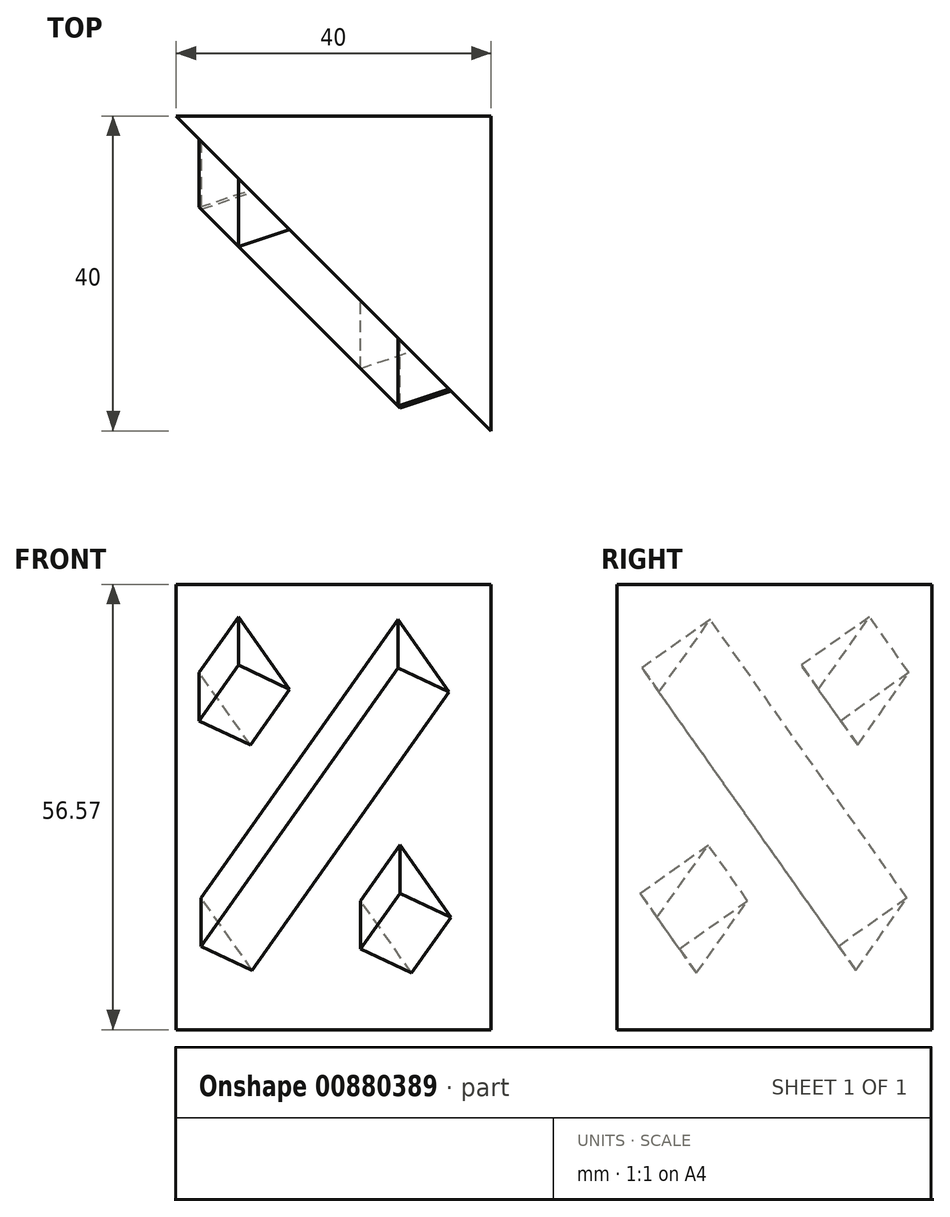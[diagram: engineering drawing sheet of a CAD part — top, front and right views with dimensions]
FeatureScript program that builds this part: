
annotation { "Feature Type Name" : "Feature", "Feature Type Description" : "" }
export const myFeature = defineFeature(function(context is Context, id is Id, definition is map)
    precondition{}
    {
        {
            var Q0;
            Q0=qCreatedBy(makeId("Top.planeOp"),FACE);
            var sketch = newSketch(context, id + "F0", { "sketchPlane" : qUnion([Q0])});
            skLineSegment(sketch, "E0.bottom", {"start": v(20, 20) * mm, "end": v(-20, 20) * mm});
            skLineSegment(sketch, "E0.top", {"start": v(20, -20) * mm, "end": v(-20, -20) * mm});
            skLineSegment(sketch, "E0.left", {"start": v(20, 20) * mm, "end": v(20, -20) * mm});
            skLineSegment(sketch, "E0.right", {"start": v(-20, 20) * mm, "end": v(-20, -20) * mm});
            skPoint(sketch, "E0.middle", {"position": v(0, 0) * mm});
            skLineSegment(sketch, "E1", {"start": v(-20, 20) * mm, "end": v(20, -20) * mm});
            skSolve(sketch);
        }
        {
            var Q0;
            Q0=makeQuery(id+"F0.imprint","IMPRINT",FACE,{"disambiguationData":[TD([[makeQuery(id+"F0.imprint","IMPRINT",EDGE,{"derivedFrom":sQuery(id+"F0.wireOp",EDGE,"E0.bottom")}),1.0]])]});
            extrude(context, id + "F1", {"entities" : qUnion([Q0]), "depth" : (40 * sqrt(2)) * mm, "offsetDistance" : 25 * mm});
        }
        {
            var Q0;
            Q0=makeQuery(id+"F1.opExtrude","SWEPT_FACE",FACE,{"disambiguationData":[OSD([sQuery(id+"F0.wireOp",EDGE,"E1")])]});
            var sketch = newSketch(context, id + "F2", { "sketchPlane" : qUnion([Q0])});
            skLineSegment(sketch, "E2", {"start": v(28.28, 0) * mm, "end": v(-28.28, 56.57) * mm});
            skSolve(sketch);
        }
        {
            var Q0;
            Q0=sQuery(id+"F2.wireOp",EDGE,"E2");
            var Q1;
            Q1=makeQuery(id+"F2.imprint","IMPRINT",FACE,{"disambiguationData":[TD([[makeQuery(id+"F2.imprint","IMPRINT",EDGE,{"derivedFrom":sQuery(id+"F2.wireOp",EDGE,"E2")}),-1.0]])]});
            cPlane(context, id + "F3", {"entities" : qUnion([Q0, Q1]), "cplaneType" : CPlaneType.LINE_ANGLE, "offset" : 25 * mm, "angle" : 90 * degree, "width" : 150 * mm, "height" : 150 * mm});
        }
        {
            var Q0;
            Q0=qCreatedBy(id+"F3.planeOp",FACE);
            var sketch = newSketch(context, id + "F4", { "sketchPlane" : qUnion([Q0])});
            skLineSegment(sketch, "E3", {"start": v(-28.38, -40.13) * mm, "end": v(-28.38, -29.52) * mm});
            skLineSegment(sketch, "E4", {"start": v(-28.38, -29.52) * mm, "end": v(-20.88, -29.52) * mm});
            skLineSegment(sketch, "E5", {"start": v(-20.88, -29.52) * mm, "end": v(-16.55, -23.4) * mm});
            skLineSegment(sketch, "E6", {"start": v(-16.55, -23.4) * mm, "end": v(-16.55, -12.8) * mm});
            skLineSegment(sketch, "E7", {"start": v(-16.55, -12.8) * mm, "end": v(-9.05, -12.8) * mm});
            skLineSegment(sketch, "E8", {"start": v(-4.72, 3.94) * mm, "end": v(2.78, 3.94) * mm});
            skLineSegment(sketch, "E9", {"start": v(-34.64, -48.99) * mm, "end": v(-28.38, -40.13) * mm});
            skLineSegment(sketch, "E10", {"start": v(2.78, 3.94) * mm, "end": v(11.55, 16.33) * mm});
            skLineSegment(sketch, "E11", {"start": v(-4.72, 3.94) * mm, "end": v(-4.72, -6.67) * mm});
            skLineSegment(sketch, "E12", {"start": v(-4.72, -6.67) * mm, "end": v(-9.05, -12.8) * mm});
            skLineSegment(sketch, "E13.0", {"start": v(11.55, 16.33) * mm, "end": v(-34.64, -48.99) * mm});
            skLineSegment(sketch, "E14", {"start": v(-16.55, -12.8) * mm, "end": v(-11.55, -16.33) * mm});
            skSolve(sketch);
        }
        {
            var Q0;
            {var subQ0=sQuery(id+"F4.wireOp",EDGE,"E3");Q0=makeQuery(id+"F4.imprint","IMPRINT",FACE,{"disambiguationData":[TD([[makeQuery(id+"F4.imprint","IMPRINT",EDGE,{"derivedFrom":subQ0}),-1.0]])]});}
            var Q1;
            {var subQ0=sQuery(id+"F4.wireOp",EDGE,"E8");Q1=makeQuery(id+"F4.imprint","IMPRINT",FACE,{"disambiguationData":[TD([[makeQuery(id+"F4.imprint","IMPRINT",EDGE,{"derivedFrom":subQ0}),-1.0]])]});}
            extrude(context, id + "F5", {"entities" : qUnion([Q0, Q1]), "operationType" : NewBodyOperationType.ADD, "endBound" : BoundingType.SYMMETRIC, "depth" : 10 * mm, "offsetDistance" : 25 * mm});
        }
        {
            var Q0;
            {var subQ0=sQuery(id+"F4.wireOp",EDGE,"E6");Q0=makeQuery(id+"F4.imprint","IMPRINT",FACE,{"disambiguationData":[TD([[makeQuery(id+"F4.imprint","IMPRINT",EDGE,{"derivedFrom":subQ0}),-1.0]])]});}
            var Q1;
            {var subQ0=sQuery(id+"F4.wireOp",EDGE,"E7");Q1=makeQuery(id+"F4.imprint","IMPRINT",FACE,{"disambiguationData":[TD([[makeQuery(id+"F4.imprint","IMPRINT",EDGE,{"derivedFrom":subQ0}),-1.0]])]});}
            extrude(context, id + "F6", {"entities" : qUnion([Q0, Q1]), "operationType" : NewBodyOperationType.ADD, "endBound" : BoundingType.SYMMETRIC, "depth" : 50 * mm, "offsetDistance" : 25 * mm});
        }
    });
